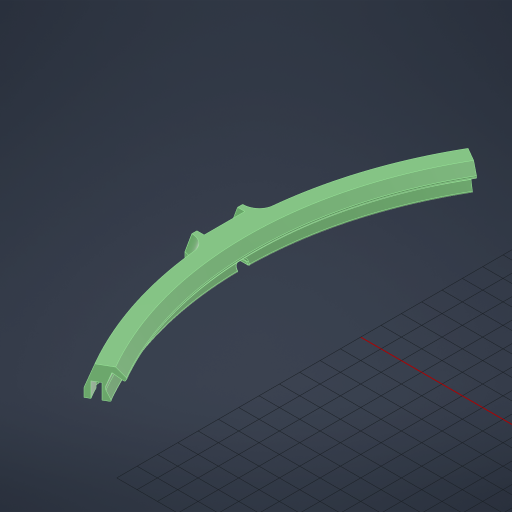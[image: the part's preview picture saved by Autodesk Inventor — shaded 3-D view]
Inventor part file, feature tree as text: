
AUTODESK INVENTOR PART (.ipt)
format: ipt  version: 2023.2 (Build 272271030, 271C)  size: 484,864 bytes
history: native  units: mm
features: sketch x4, extrude x4, revolve x2, hole x2, fillet x2, chamfer x2, projected_geometry x2, other x1
ambient origin geometry x8: Origin, YZ Plane, XZ Plane, XY Plane, X Axis, Y Axis, Z Axis, Center Point
bodies: Volumenkörper1 (feature_tree)
feature tree (19):
  sketch  "Skizze1"  dims[d1=30.0mm d5=1.0mm]
  revolve  "Umdrehung1"
  revolve  "Umdrehung2"
  sketch  "Skizze2"  dims[d9=135.0deg d14=8.5mm]
  hole  "Bohrung1"  [1 undecoded]
  extrude  "Extrusion4"  Depth=8.5mm
  sketch  "Skizze4"  dims[d18=360.0mm d25=50.0mm]
  extrude  "Extrusion1"  Depth=50.0mm
  extrude  "Extrusion2"  TaperAngle=60.0deg  [1 undecoded]
  fillet  "Rundung1"  Radius=15.0mm
  chamfer  "Fase1"  Distance=3.5mm
  sketch  "Skizze5"  dims[d26=225.0mm d30=60.0deg d31=15.0mm d40=3.5mm d41=120.0mm d42=35.0mm d43=1.0mm d47=6.0mm d50=11.362634mm d54=15.0mm d59=2.094395mm d60=27.925268mm d66=15.0mm d70=4.5mm d71=6.0mm d73=3.2mm d74=3.0mm d75=6.0mm d76=6.0mm d77=6.0mm d79=4.5mm d80=15.0mm d81=2.0mm d82=8.0mm d83=120.0mm d84=30.0deg d85=0.436332mm d86=1.745329mm d87=0.436332mm d88=1.745329mm d89=4.5mm d90=4.5mm d91=6.0mm d92=4.0mm d93=2.0mm d94=90.0deg d95=6.0mm d96=0.0mm d100=370.0mm d101=18.0mm d102=50.0mm d103=0.0mm d104=6.0mm d105=4.0mm d106=40.0mm d107=0.0mm d108=15.0mm d110=6.85mm d111=2.0mm d112=12.217305mm d113=4.5mm d114=16.0mm d115=10.0mm d116=4.5mm d117=6.0mm d118=4.0mm d119=2.0mm d120=90.0deg d121=7.0mm d122=0.0mm d123=1.0mm d124=2.0mm d125=45.0deg d126=6.0mm d127=10.0mm d128=0.0mm d129=0.0mm d130=1.0mm d131=10.0mm d132=0.0mm d133=0.0mm]
  hole  "Bohrung2"  [1 undecoded]
  extrude  "Extrusion3"  Depth=10.0mm
  chamfer  "Fase2"  Distance=1.0mm
  fillet  "Rundung3"  Radius=6.0mm
  projected_geometry  "Projizierte Kontur1"
  projected_geometry  "Projizierte Kontur2"
  other  "Schnittkanten projizieren1"
note: 3 required parameter values undecoded (feature->parameter linkage not recoverable at this tier; creation-order binding heuristic only, values carry confidence <= 0.55)
